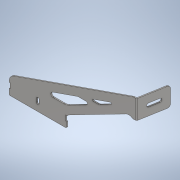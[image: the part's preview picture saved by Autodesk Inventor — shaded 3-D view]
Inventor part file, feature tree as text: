
AUTODESK INVENTOR PART (.ipt)
format: ipt  version: 2020 (Build 240168000, 168)  size: 442,368 bytes
history: native  units: mm
features: other x3, extrude x1, plane x1
ambient origin geometry x8: Origin, YZ Plane, XZ Plane, XY Plane, X Axis, Y Axis, Z Axis, Center Point
bodies: Body1 (feature_tree)
feature tree (5):
  other  "實體1"
  extrude  "擠出1"  Depth=130.0mm
  other  "折彎零件1"
  plane  "工作平面1"
  other  "定義1"
